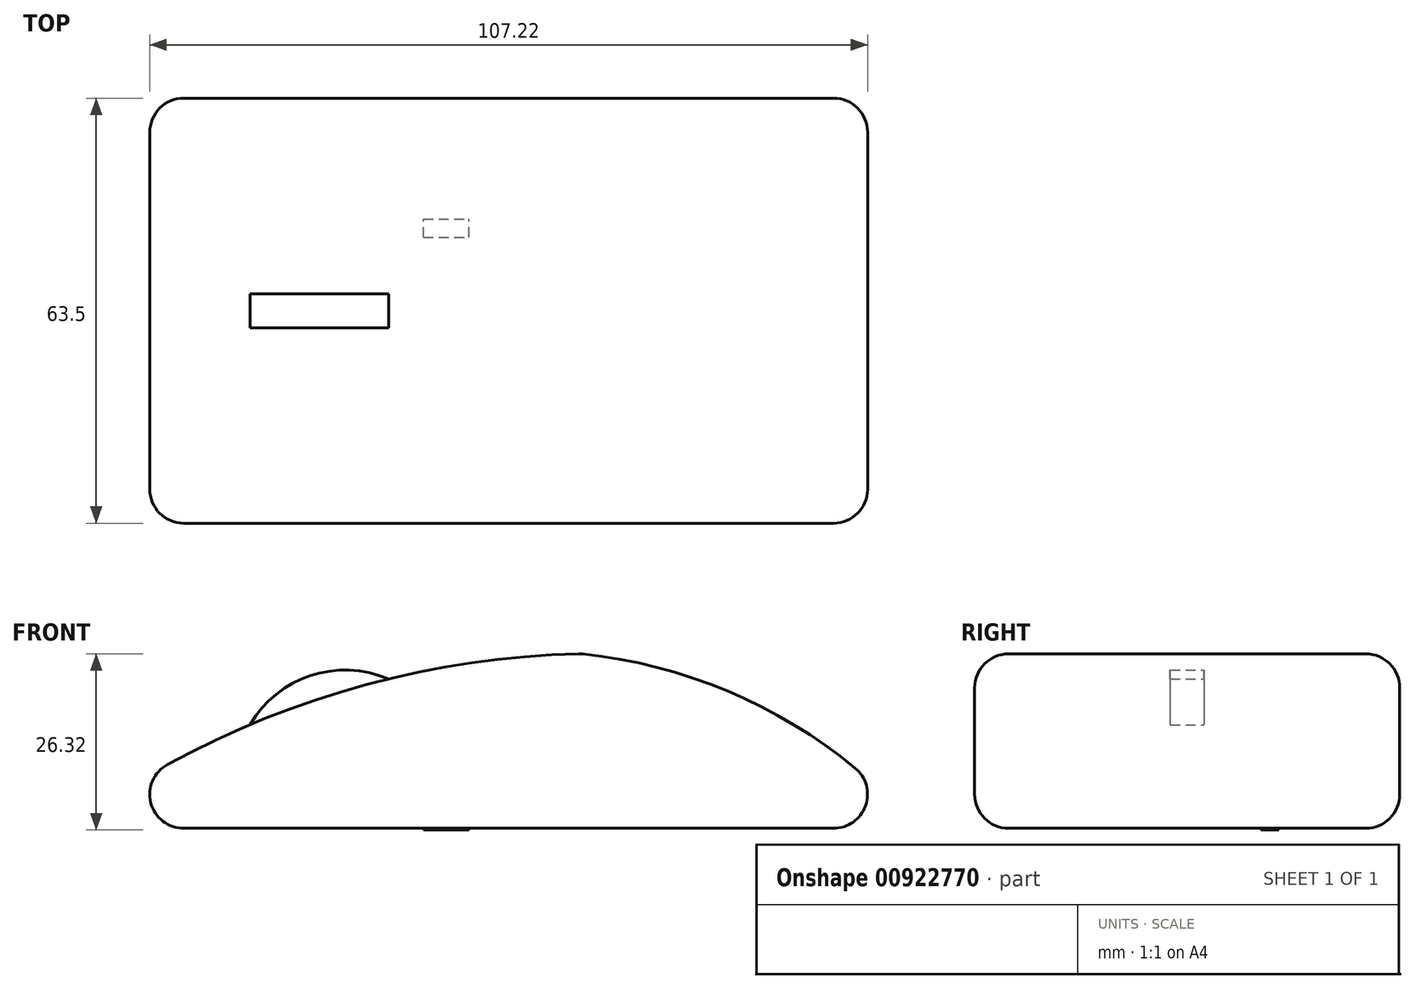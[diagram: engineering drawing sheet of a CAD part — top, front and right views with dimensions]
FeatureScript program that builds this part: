
annotation { "Feature Type Name" : "Feature", "Feature Type Description" : "" }
export const myFeature = defineFeature(function(context is Context, id is Id, definition is map)
    precondition{}
    {
        {
            var Q0;
            Q0=qCreatedBy(makeId("Front.planeOp"),FACE);
            var sketch = newSketch(context, id + "F0", { "sketchPlane" : qUnion([Q0])});
            skLineSegment(sketch, "E0", {"start": v(-53.26, -21) * mm, "end": v(73.74, -21) * mm});
            skArc(sketch, "E1", {"start": v(73.74, -21) * mm, "mid": v(51.12, -3.16) * mm, "end": v(23.51, 5.07) * mm});
            skArc(sketch, "E2", {"start": v(23.51, 5.07) * mm, "mid": v(-16.87, -2.09) * mm, "end": v(-53.26, -21) * mm});
            skArc(sketch, "E3", {"start": v(-5.21, 1.3) * mm, "mid": v(-16.84, 1.81) * mm, "end": v(-25.9, -5.52) * mm});
            skSolve(sketch);
        }
        {
            var Q0;
            {var subQ5=sQuery(id+"F0.wireOp",EDGE,"E0");Q0=makeQuery(id+"F0.imprint","IMPRINT",FACE,{"disambiguationData":[TD([[makeQuery(id+"F0.imprint","IMPRINT",EDGE,{"derivedFrom":subQ5}),1.0]])]});}
            extrude(context, id + "F1", {"entities" : qUnion([Q0]), "depth" : 31.75 * mm, "offsetDistance" : 25.4 * mm, "hasSecondDirection" : true, "secondDirectionOppositeDirection" : true, "secondDirectionDepth" : 31.75 * mm});
        }
        {
            var Q0;
            {var subQ0=sQuery(id+"F0.wireOp",EDGE,"E3");Q0=makeQuery(id+"F0.imprint","IMPRINT",FACE,{"disambiguationData":[TD([[makeQuery(id+"F0.imprint","IMPRINT",EDGE,{"derivedFrom":subQ0}),1.0]])]});}
            extrude(context, id + "F2", {"entities" : qUnion([Q0]), "operationType" : NewBodyOperationType.ADD, "depth" : 2.54 * mm, "offsetDistance" : 25.4 * mm, "hasSecondDirection" : true, "secondDirectionOppositeDirection" : true, "secondDirectionDepth" : 2.54 * mm});
        }
        {
            var Q0;
            Q0=makeQuery(id+"F1.opExtrude","SWEPT_EDGE",EDGE,{"disambiguationData":[OSD([sQuery(id+"F0.wireOp",EDGE,"E0"),sQuery(id+"F0.wireOp",EDGE,"E2")])]});
            var Q1;
            Q1=makeQuery(id+"F1.opExtrude","CAP_FACE",FACE,{"disambiguationData":[OSD([sQuery(id+"F0.wireOp",EDGE,"E0"),sQuery(id+"F0.wireOp",EDGE,"E1"),sQuery(id+"F0.wireOp",EDGE,"E2")])],"isStart":false});
            var Q2;
            Q2=makeQuery(id+"F1.opExtrude","CAP_FACE",FACE,{"disambiguationData":[OSD([sQuery(id+"F0.wireOp",EDGE,"E0"),sQuery(id+"F0.wireOp",EDGE,"E1"),sQuery(id+"F0.wireOp",EDGE,"E2")])],"isStart":true});
            var Q3;
            Q3=makeQuery(id+"F1.opExtrude","SWEPT_FACE",FACE,{"disambiguationData":[OSD([sQuery(id+"F0.wireOp",EDGE,"E1")])]});
            var Q4;
            Q4=makeQuery(id+"F1.opExtrude","SWEPT_EDGE",EDGE,{"disambiguationData":[OSD([sQuery(id+"F0.wireOp",EDGE,"E1"),sQuery(id+"F0.wireOp",EDGE,"E2")])]});
            fillet(context, id + "F3", {"entities" : qUnion([Q0, Q1, Q2, Q3, Q4]), "radius" : 5.08 * mm, "tangentPropagation" : true, "allowEdgeOverflow" : false});
        }
        {
            var Q0;
            Q0=makeQuery(id+"F1.opExtrude","SWEPT_FACE",FACE,{"disambiguationData":[OSD([sQuery(id+"F0.wireOp",EDGE,"E0")])]});
            var sketch = newSketch(context, id + "F4", { "sketchPlane" : qUnion([Q0])});
            skLineSegment(sketch, "E4.bottom", {"start": v(-35.73, -2.91) * mm, "end": v(-17.73, -2.91) * mm});
            skLineSegment(sketch, "E4.top", {"start": v(-35.73, 2.9) * mm, "end": v(-17.73, 2.9) * mm});
            skLineSegment(sketch, "E4.left", {"start": v(-35.73, -2.91) * mm, "end": v(-35.73, 2.9) * mm});
            skLineSegment(sketch, "E4.right", {"start": v(-17.73, -2.91) * mm, "end": v(-17.73, 2.9) * mm});
            skLineSegment(sketch, "E5.bottom", {"start": v(-17.73, 0) * mm, "end": v(-1.12, 0) * mm});
            skLineSegment(sketch, "E5.top", {"start": v(-17.73, 0) * mm, "end": v(-1.12, 0) * mm});
            skLineSegment(sketch, "E5.left", {"start": v(-17.73, 0) * mm, "end": v(-17.73, 0) * mm});
            skLineSegment(sketch, "E5.right", {"start": v(-1.12, 0) * mm, "end": v(-1.12, 0) * mm});
            skLineSegment(sketch, "E6.bottom", {"start": v(-35.73, 0) * mm, "end": v(-48.83, 0) * mm});
            skLineSegment(sketch, "E6.top", {"start": v(-35.73, 0) * mm, "end": v(-48.83, 0) * mm});
            skLineSegment(sketch, "E6.left", {"start": v(-35.73, 0) * mm, "end": v(-35.73, 0) * mm});
            skLineSegment(sketch, "E6.right", {"start": v(-48.83, 0) * mm, "end": v(-48.83, 0) * mm});
            skSolve(sketch);
        }
        {
            var Q0;
            {var subQ3=sQuery(id+"F4.wireOp",EDGE,"E4.bottom");Q0=makeQuery(id+"F4.imprint","IMPRINT",FACE,{"disambiguationData":[TD([[makeQuery(id+"F4.imprint","IMPRINT",EDGE,{"derivedFrom":subQ3}),-1.0]])]});}
            var sketch = newSketch(context, id + "F5", { "sketchPlane" : qUnion([Q0])});
            skLineSegment(sketch, "E7.bottom", {"start": v(0, -11) * mm, "end": v(6.83, -11) * mm});
            skLineSegment(sketch, "E7.top", {"start": v(0, -13.71) * mm, "end": v(6.83, -13.71) * mm});
            skLineSegment(sketch, "E7.left", {"start": v(0, -11) * mm, "end": v(0, -13.71) * mm});
            skLineSegment(sketch, "E7.right", {"start": v(6.83, -11) * mm, "end": v(6.83, -13.71) * mm});
            skSolve(sketch);
        }
        {
            var Q0;
            Q0=makeQuery(id+"F5.imprint","IMPRINT",FACE,{"disambiguationData":[TD([[makeQuery(id+"F5.imprint","IMPRINT",EDGE,{"derivedFrom":sQuery(id+"F5.wireOp",EDGE,"E7.bottom")}),-1.0]])]});
            extrude(context, id + "F6", {"entities" : qUnion([Q0]), "operationType" : NewBodyOperationType.ADD, "depth" : 0.25 * mm, "offsetDistance" : 25.4 * mm});
        }
    });
